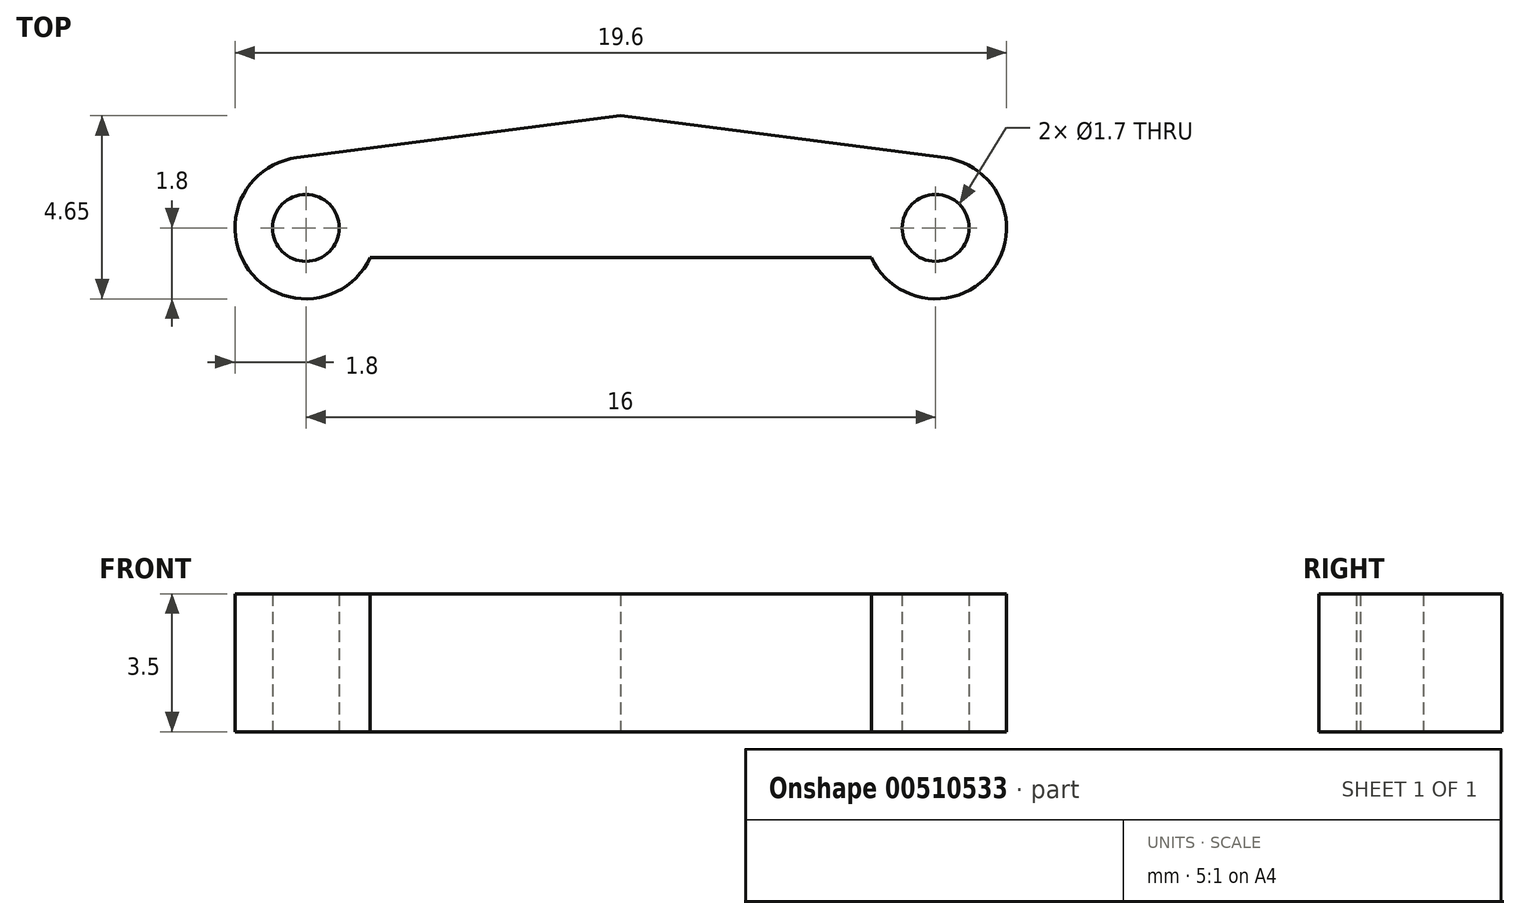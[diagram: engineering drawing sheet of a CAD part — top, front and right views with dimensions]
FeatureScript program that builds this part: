
annotation { "Feature Type Name" : "Feature", "Feature Type Description" : "" }
export const myFeature = defineFeature(function(context is Context, id is Id, definition is map)
    precondition{}
    {
        {
            var Q0;
            Q0=qCreatedBy(makeId("Top.planeOp"),FACE);
            var sketch = newSketch(context, id + "F0", { "sketchPlane" : qUnion([Q0])});
            skPoint(sketch, "E0.middle", {"position": v(0, 0) * mm});
            skArc(sketch, "E1", {"start": v(6.36, -0.75) * mm, "mid": v(9.45, -1.07) * mm, "end": v(8.23, 1.79) * mm});
            skArc(sketch, "E2", {"start": v(-8.23, 1.79) * mm, "mid": v(-9.45, -1.07) * mm, "end": v(-6.36, -0.75) * mm});
            skCircle(sketch, "E3", {"center": v(-8, 0) * mm, "radius": 0.85 * mm});
            skCircle(sketch, "E4", {"center": v(8, 0) * mm, "radius": 0.85 * mm});
            skLineSegment(sketch, "E5", {"start": v(-6.36, -0.75) * mm, "end": v(6.36, -0.75) * mm});
            skPoint(sketch, "E6", {"position": v(0, 2.85) * mm});
            skLineSegment(sketch, "E7", {"start": v(0, 2.85) * mm, "end": v(-8.23, 1.79) * mm});
            skLineSegment(sketch, "E8", {"start": v(0, 2.85) * mm, "end": v(8.23, 1.79) * mm});
            skSolve(sketch);
        }
        {
            var Q0;
            Q0=makeQuery(id+"F0.imprint","IMPRINT",FACE,{"disambiguationData":[TD([[makeQuery(id+"F0.imprint","IMPRINT",EDGE,{"derivedFrom":sQuery(id+"F0.wireOp",EDGE,"E1")}),1.0]])]});
            extrude(context, id + "F1", {"entities" : qUnion([Q0]), "depth" : 3.5 * mm});
        }
    });
